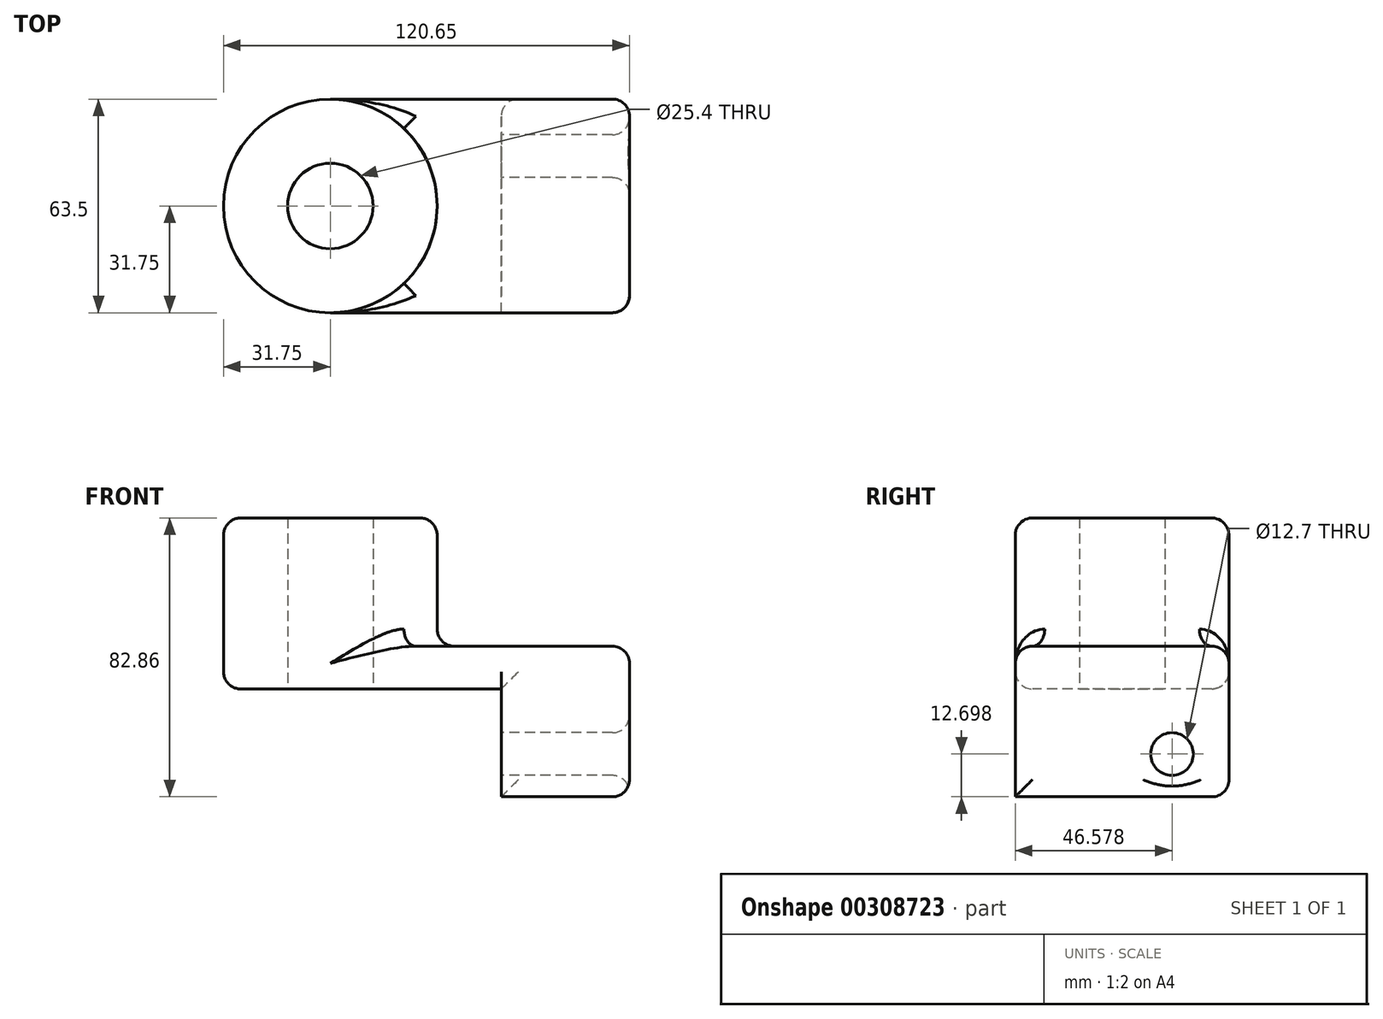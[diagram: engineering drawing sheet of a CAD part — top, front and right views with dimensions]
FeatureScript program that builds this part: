
annotation { "Feature Type Name" : "Feature", "Feature Type Description" : "" }
export const myFeature = defineFeature(function(context is Context, id is Id, definition is map)
    precondition{}
    {
        {
            var Q0;
            Q0=qCreatedBy(makeId("Top.planeOp"),FACE);
            var sketch = newSketch(context, id + "F0", { "sketchPlane" : qUnion([Q0])});
            skLineSegment(sketch, "E0.bottom", {"start": v(-38.1, 31.75) * mm, "end": v(38.1, 31.75) * mm});
            skLineSegment(sketch, "E0.top", {"start": v(-38.1, -31.75) * mm, "end": v(38.1, -31.75) * mm});
            skLineSegment(sketch, "E0.left", {"start": v(-38.1, 31.75) * mm, "end": v(-38.1, -31.75) * mm});
            skLineSegment(sketch, "E0.right", {"start": v(38.1, 31.75) * mm, "end": v(38.1, -31.75) * mm});
            skPoint(sketch, "E0.middle", {"position": v(0, 0) * mm});
            skCircle(sketch, "E1", {"center": v(-38.1, 0) * mm, "radius": 31.75 * mm});
            skCircle(sketch, "E2", {"center": v(-38.1, 0) * mm, "radius": 12.7 * mm});
            skSolve(sketch);
        }
        {
            var Q0;
            Q0 = qSketchRegion(id + "F0", true);
            extrude(context, id + "F1", {"entities" : qUnion([Q0]), "depth" : 12.7 * mm});
        }
        {
            var Q0;
            {var subQ1=sQuery(id+"F0.wireOp",EDGE,"E0.left");var subQ3=sQuery(id+"F0.wireOp",EDGE,"E2");var subQ4=makeQuery(id+"F0.imprint","INTERSECT",VERTEX,{"disambiguationData":[OD(0.0)],"derivedFrom":[subQ1,subQ3]});Q0=makeQuery(id+"F0.imprint","IMPRINT",FACE,{"disambiguationData":[TD([[makeQuery(id+"F0.imprint","IMPRINT",EDGE,{"disambiguationData":[TD([[subQ4,-1.0]])],"derivedFrom":subQ3}),-1.0]])]});}
            var Q1;
            {var subQ1=sQuery(id+"F0.wireOp",EDGE,"E0.left");var subQ3=sQuery(id+"F0.wireOp",EDGE,"E2");var subQ4=makeQuery(id+"F0.imprint","INTERSECT",VERTEX,{"disambiguationData":[OD(0.0)],"derivedFrom":[subQ1,subQ3]});Q1=makeQuery(id+"F0.imprint","IMPRINT",FACE,{"disambiguationData":[TD([[makeQuery(id+"F0.imprint","IMPRINT",EDGE,{"disambiguationData":[TD([[subQ4,1.0]])],"derivedFrom":subQ3}),-1.0]])]});}
            extrude(context, id + "F2", {"entities" : qUnion([Q0, Q1]), "operationType" : NewBodyOperationType.ADD, "depth" : 50.8 * mm});
        }
        {
            var Q0;
            Q0=makeQuery(id+"F1.opExtrude","SWEPT_FACE",FACE,{"disambiguationData":[OSD([sQuery(id+"F0.wireOp",EDGE,"E0.right")])]});
            var sketch = newSketch(context, id + "F3", { "sketchPlane" : qUnion([Q0])});
            skLineSegment(sketch, "E3.bottom", {"start": v(-31.75, 12.7) * mm, "end": v(31.75, 12.7) * mm});
            skLineSegment(sketch, "E3.top", {"start": v(-31.75, -32.06) * mm, "end": v(31.75, -32.06) * mm});
            skLineSegment(sketch, "E3.left", {"start": v(-31.75, 12.7) * mm, "end": v(-31.75, -32.06) * mm});
            skLineSegment(sketch, "E3.right", {"start": v(31.75, 12.7) * mm, "end": v(31.75, -32.06) * mm});
            skCircle(sketch, "E4", {"center": v(-14.83, -19.36) * mm, "radius": 6.35 * mm});
            skLineSegment(sketch, "E5", {"start": v(0, 0) * mm, "end": v(0, -56.2) * mm, "construction": true});
            skPoint(sketch, "E5.endSnap0", {"position": v(0, -32.06) * mm});
            skCircle(sketch, "E6.MirrorC", {"center": v(14.83, -19.36) * mm, "radius": 6.35 * mm});
            skSolve(sketch);
        }
        {
            var Q0;
            {var subQ2=sQuery(id+"F3.wireOp",EDGE,"E3.top");Q0=makeQuery(id+"F3.imprint","IMPRINT",FACE,{"disambiguationData":[TD([[makeQuery(id+"F3.imprint","IMPRINT",EDGE,{"derivedFrom":subQ2}),1.0]])]});}
            var Q1;
            Q1=makeQuery(id+"F3.imprint","IMPRINT",FACE,{"disambiguationData":[TD([[makeQuery(id+"F3.imprint","IMPRINT",EDGE,{"derivedFrom":sQuery(id+"F3.wireOp",EDGE,"E6.MirrorC")}),-1.0]])]});
            var Q2;
            {var subQ0=sQuery(id+"F3.wireOp",EDGE,"E3.bottom");Q2=makeQuery(id+"F3.imprint","IMPRINT",FACE,{"disambiguationData":[TD([[makeQuery(id+"F3.imprint","IMPRINT",EDGE,{"derivedFrom":subQ0}),1.0]])]});}
            var Q3;
            Q3=makeQuery(id+"F3.imprint","IMPRINT",FACE,{"disambiguationData":[TD([[makeQuery(id+"F3.imprint","IMPRINT",EDGE,{"derivedFrom":sQuery(id+"F3.wireOp",EDGE,"E4")}),1.0]])]});
            var Q4;
            Q4=makeQuery(id+"F1.opExtrude","SWEPT_FACE",FACE,{"disambiguationData":[OSD([sQuery(id+"F0.wireOp",EDGE,"E0.right")])]});
            extrude(context, id + "F4", {"entities" : qUnion([Q0, Q1, Q2, Q3, Q4]), "operationType" : NewBodyOperationType.ADD, "depth" : 12.7 * mm});
        }
        {
            var Q0;
            Q0=makeQuery(id+"F4.boolean.opBoolean","MERGE",FACE,{"derivedFrom":[makeQuery(id+"F4.opExtrude","CAP_FACE",FACE,{"disambiguationData":[OSD([sQuery(id+"F0.wireOp",EDGE,"E0.right")])],"isStart":false}),makeQuery(id+"F4.opExtrude","CAP_FACE",FACE,{"disambiguationData":[OSD([sQuery(id+"F3.wireOp",EDGE,"E3.bottom"),sQuery(id+"F3.wireOp",EDGE,"E3.top"),sQuery(id+"F3.wireOp",EDGE,"E3.left"),sQuery(id+"F3.wireOp",EDGE,"E3.right")])],"isStart":false})]});
            var sketch = newSketch(context, id + "F5", { "sketchPlane" : qUnion([Q0])});
            skSolve(sketch);
        }
        {
            var Q0;
            Q0=makeQuery(id+"F5.imprint","IMPRINT",FACE,{"disambiguationData":[TD([[makeQuery(id+"F5.imprint","IMPRINT",EDGE,{"derivedFrom":makeQuery(id+"F4.opExtrude","CAP_EDGE",EDGE,{"disambiguationData":[OSD([sQuery(id+"F3.wireOp",EDGE,"E3.top")])],"isStart":false})}),1.0]])]});
            var sketch = newSketch(context, id + "F6", { "sketchPlane" : qUnion([Q0])});
            skCircle(sketch, "E7", {"center": v(-17.28, -12.3) * mm, "radius": 6.35 * mm});
            skLineSegment(sketch, "E8", {"start": v(0, 13.02) * mm, "end": v(0, -83.05) * mm, "construction": true});
            skCircle(sketch, "E9.MirrorC", {"center": v(17.28, -12.3) * mm, "radius": 6.35 * mm});
            skSolve(sketch);
        }
        {
            var Q0;
            Q0=sQuery(id+"F6.wireOp",EDGE,"E7");
            var Q1;
            Q1=sQuery(id+"F6.wireOp",EDGE,"E9.MirrorC");
            extrude(context, id + "F7", {"bodyType" : ToolBodyType.SURFACE, "surfaceEntities" : qUnion([Q0, Q1]), "oppositeDirection" : true, "depth" : 13.46 * mm});
        }
        {
            var Q0;
            Q0=makeQuery(id+"F4.boolean.opBoolean","MERGE",FACE,{"derivedFrom":[makeQuery(id+"F4.opExtrude","CAP_FACE",FACE,{"disambiguationData":[OSD([sQuery(id+"F0.wireOp",EDGE,"E0.right")])],"isStart":true}),makeQuery(id+"F4.opExtrude","CAP_FACE",FACE,{"disambiguationData":[OSD([sQuery(id+"F3.wireOp",EDGE,"E3.bottom"),sQuery(id+"F3.wireOp",EDGE,"E3.top"),sQuery(id+"F3.wireOp",EDGE,"E3.left"),sQuery(id+"F3.wireOp",EDGE,"E3.right")])],"isStart":true})]});
            extrude(context, id + "F8", {"entities" : qUnion([Q0]), "operationType" : NewBodyOperationType.ADD, "depth" : 25.4 * mm});
        }
        {
            var Q0;
            {var subQ0=sQuery(id+"F0.wireOp",EDGE,"E0.right");Q0=makeQuery(id+"F4.boolean.opBoolean","MERGE",FACE,{"derivedFrom":[makeQuery(id+"F1.opExtrude","CAP_FACE",FACE,{"disambiguationData":[OSD([sQuery(id+"F0.wireOp",EDGE,"E0.bottom"),sQuery(id+"F0.wireOp",EDGE,"E0.top"),subQ0,sQuery(id+"F0.wireOp",EDGE,"E1"),sQuery(id+"F0.wireOp",EDGE,"E2")])],"isStart":false}),makeQuery(id+"F4.opExtrude","SWEPT_FACE",FACE,{"disambiguationData":[OSD([subQ0]),TDD([makeQuery(id+"F1.opExtrude","CAP_EDGE",EDGE,{"disambiguationData":[OSD([subQ0])],"isStart":false})])]})]});}
            var Q1;
            Q1=makeQuery(id+"F4.boolean.opBoolean","MERGE",FACE,{"derivedFrom":[makeQuery(id+"F4.opExtrude","CAP_FACE",FACE,{"disambiguationData":[OSD([sQuery(id+"F0.wireOp",EDGE,"E0.right")])],"isStart":false}),makeQuery(id+"F4.opExtrude","CAP_FACE",FACE,{"disambiguationData":[OSD([sQuery(id+"F3.wireOp",EDGE,"E3.bottom"),sQuery(id+"F3.wireOp",EDGE,"E3.top"),sQuery(id+"F3.wireOp",EDGE,"E3.left"),sQuery(id+"F3.wireOp",EDGE,"E3.right")])],"isStart":false})]});
            var Q2;
            {var subQ0=sQuery(id+"F3.wireOp",EDGE,"E3.right");var subQ1=sQuery(id+"F0.wireOp",EDGE,"E0.right");var subQ2=sQuery(id+"F0.wireOp",EDGE,"E0.bottom");Q2=makeQuery(id+"F8.boolean.opBoolean","MERGE",FACE,{"derivedFrom":[makeQuery(id+"F4.boolean.opBoolean","MERGE",FACE,{"derivedFrom":[makeQuery(id+"F1.opExtrude","SWEPT_FACE",FACE,{"disambiguationData":[OSD([subQ2])]}),makeQuery(id+"F4.opExtrude","SWEPT_FACE",FACE,{"disambiguationData":[OSD([subQ2,subQ1])]}),makeQuery(id+"F4.opExtrude","SWEPT_FACE",FACE,{"disambiguationData":[OSD([subQ0])]})]}),makeQuery(id+"F8.opExtrude","SWEPT_FACE",FACE,{"disambiguationData":[OSD([subQ2,subQ1,subQ0])]})]});}
            var Q3;
            {var subQ0=sQuery(id+"F0.wireOp",EDGE,"E1");Q3=makeQuery(id+"F2.boolean.opBoolean","MERGE",FACE,{"derivedFrom":[makeQuery(id+"F1.opExtrude","SWEPT_FACE",FACE,{"disambiguationData":[OSD([subQ0])]}),makeQuery(id+"F2.opExtrude","SWEPT_FACE",FACE,{"disambiguationData":[OSD([subQ0])]})]});}
            fillet(context, id + "F9", {"entities" : qUnion([Q0, Q1, Q2, Q3]), "radius" : 5.08 * mm, "tangentPropagation" : true, "allowEdgeOverflow" : false});
        }
    });
